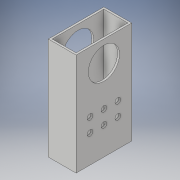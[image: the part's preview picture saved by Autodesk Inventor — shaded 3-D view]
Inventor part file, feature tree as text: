
AUTODESK INVENTOR PART (.ipt)
format: ipt  version: 2018 (Build 220112000, 112)  size: 153,600 bytes
history: native  units: in
note: dims shown in document units (in); Inventor stores cm internally (conversion verified against a paired STEP export)
features: extrude x3, sketch x3
ambient origin geometry x8: Origin, YZ Plane, XZ Plane, XY Plane, X Axis, Y Axis, Z Axis, Center Point
bodies: Solid1 (feature_tree)
feature tree (6):
  extrude  "Extrusion1"  Depth=2.0in
  extrude  "Extrusion2"  Depth=3.675in TaperAngle=0.0deg
  extrude  "Extrusion3"  Depth=1.0in
  sketch  "Sketch2"  dims[d0=1.0in d1=2.0in]
  sketch  "Sketch3"  dims[d2=0.07in d3=3.675in d4=0.0in]
  sketch  "Sketch4"  dims[d5=1.92in d6=1.0in d7=1.125in d8=1.675in d9=0.0in d10=0.5in d11=0.5in d12=0.5in d13=1.0in d14=0.5in d15=0.2031in d16=0.2031in d17=0.5in d18=0.5in d19=0.5in d20=0.2031in d21=0.2031in d22=0.5in d23=0.2031in d24=0.2031in d25=1.0in d26=0.0in]
